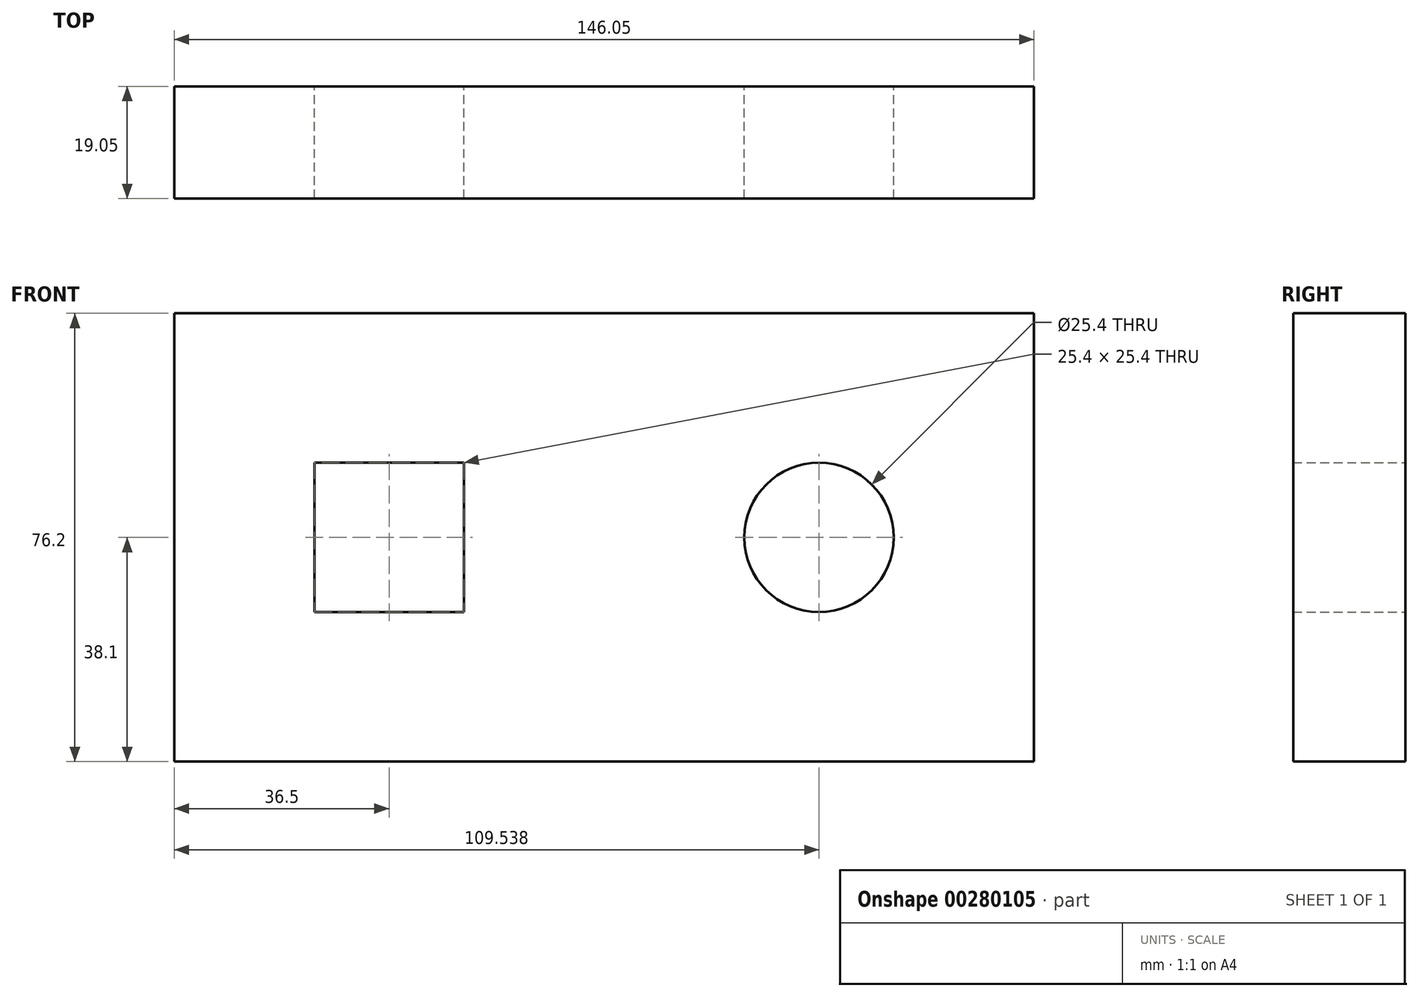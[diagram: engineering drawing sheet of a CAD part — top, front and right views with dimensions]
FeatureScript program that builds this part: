
annotation { "Feature Type Name" : "Feature", "Feature Type Description" : "" }
export const myFeature = defineFeature(function(context is Context, id is Id, definition is map)
    precondition{}
    {
        {
            var Q0;
            Q0=qCreatedBy(makeId("Front.planeOp"),FACE);
            var sketch = newSketch(context, id + "F0", { "sketchPlane" : qUnion([Q0])});
            skLineSegment(sketch, "E0.bottom", {"start": v(0, 0) * mm, "end": v(-146.05, 0) * mm});
            skLineSegment(sketch, "E0.top", {"start": v(0, 76.2) * mm, "end": v(-146.05, 76.2) * mm});
            skLineSegment(sketch, "E0.left", {"start": v(0, 0) * mm, "end": v(0, 76.2) * mm});
            skLineSegment(sketch, "E0.right", {"start": v(-146.05, 0) * mm, "end": v(-146.05, 76.2) * mm});
            skLineSegment(sketch, "E1.bottom", {"start": v(-96.85, 25.4) * mm, "end": v(-122.25, 25.4) * mm});
            skLineSegment(sketch, "E1.top", {"start": v(-96.85, 50.8) * mm, "end": v(-122.25, 50.8) * mm});
            skLineSegment(sketch, "E1.left", {"start": v(-96.85, 25.4) * mm, "end": v(-96.85, 50.8) * mm});
            skLineSegment(sketch, "E1.right", {"start": v(-122.25, 25.4) * mm, "end": v(-122.25, 50.8) * mm});
            skCircle(sketch, "E2", {"center": v(-36.51, 38.1) * mm, "radius": 12.7 * mm});
            skSolve(sketch);
        }
        {
            var Q0;
            Q0 = qSketchRegion(id + "F0", true);
            extrude(context, id + "F1", {"entities" : qUnion([Q0]), "depth" : 19.05 * mm});
        }
    });
